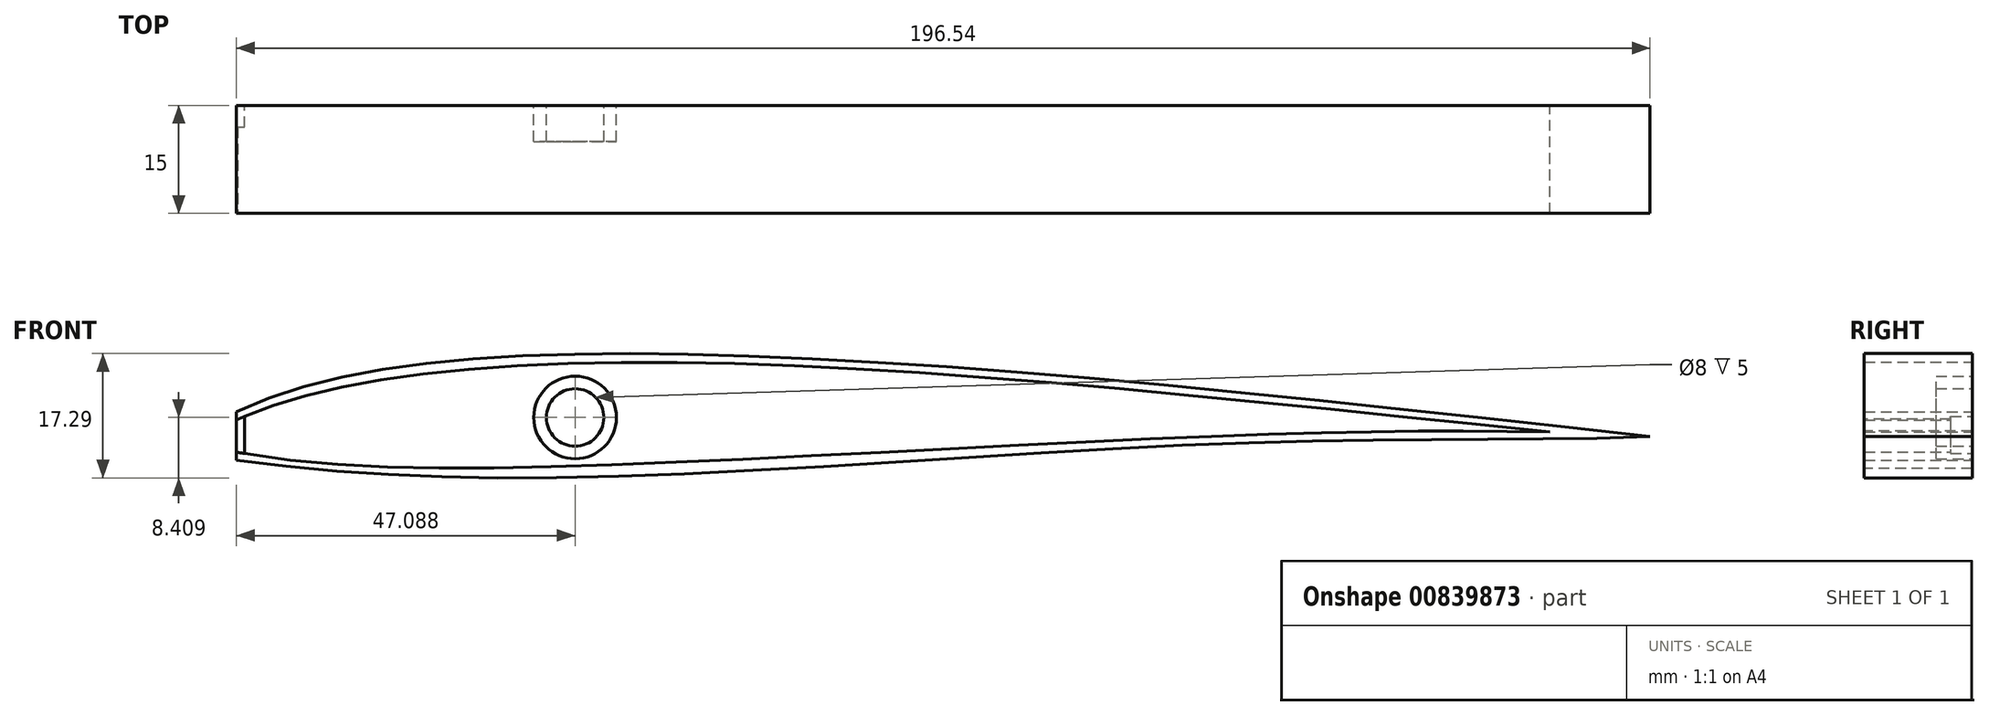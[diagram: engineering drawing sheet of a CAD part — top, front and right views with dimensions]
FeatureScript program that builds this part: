
annotation { "Feature Type Name" : "Feature", "Feature Type Description" : "" }
export const myFeature = defineFeature(function(context is Context, id is Id, definition is map)
    precondition{}
    {
        {
            var Q0;
            Q0=qCreatedBy(makeId("Front.planeOp"),FACE);
            var sketch = newSketch(context, id + "F0", { "sketchPlane" : qUnion([Q0])});
            skPoint(sketch, "E0.middle", {"position": v(0, 0) * mm});
            skFitSpline(sketch, "E1", {"points": [v(-96.98, -0.81) * mm, v(-45.24, 7.5) * mm, v(100, -4.05) * mm], "startDerivative": vector(97.58, 47.67) * mm, "endDerivative": vector(275.05, -31.29) * mm});
            skFitSpline(sketch, "E2", {"points": [v(-96.54, -7.34) * mm, v(-44.56, -9.6) * mm, v(41.7, -4.97) * mm, v(100, -4.05) * mm], "startDerivative": vector(159.07, -20.98) * mm, "endDerivative": vector(169.88, 6) * mm});
            skFitSpline(sketch, "E3", {"points": [v(-96.34, -1.64) * mm, v(-45.34, 6.27) * mm, v(86.1, -3.38) * mm], "startDerivative": vector(82.57, 38.4) * mm, "endDerivative": vector(239.73, -24.74) * mm});
            skFitSpline(sketch, "E4", {"points": [v(-97.38, -6.05) * mm, v(-44.49, -7.96) * mm, v(41.39, -3.9) * mm, v(86.1, -3.38) * mm], "startDerivative": vector(144.05, -26.77) * mm, "endDerivative": vector(139.27, -2.3) * mm});
            skLineSegment(sketch, "E5", {"start": v(-95.4, -1.21) * mm, "end": v(-95.4, -6.4) * mm});
            skLineSegment(sketch, "E6", {"start": v(-96.54, -0.6) * mm, "end": v(-96.54, -7.34) * mm});
            skFitSpline(sketch, "E7.trimOffspring", {"points": [v(-97.38, -6.05) * mm, v(-99.95, -4.56) * mm, v(-96.34, -1.64) * mm], "startDerivative": vector(-8.62, 1.03) * mm, "endDerivative": vector(10.24, 4.38) * mm});
            skPoint(sketch, "E8.trimOffspring.center.orphan", {"position": v(-96.34, -4.05) * mm});
            skPoint(sketch, "E9.1.internal.orphan", {"position": v(-101.41, -5) * mm});
            skPoint(sketch, "E10.start.orphan", {"position": v(-99.95, -4.05) * mm});
            skCircle(sketch, "E11", {"center": v(-49.45, -1.37) * mm, "radius": 4 * mm});
            skCircle(sketch, "E12", {"center": v(33.78, -1.03) * mm, "radius": 2.5 * mm});
            skLineSegment(sketch, "E13", {"start": v(-56.42, 4.45) * mm, "end": v(-56.42, -7.2) * mm});
            skLineSegment(sketch, "E14", {"start": v(-94.27, -1.68) * mm, "end": v(-94.27, -5.45) * mm});
            skFitSpline(sketch, "E15", {"points": [v(-94.27, -1.68) * mm, v(-75.44, 3) * mm, v(-56.42, 4.45) * mm], "startDerivative": vector(37.23, 13.11) * mm, "endDerivative": vector(37.06, -0.15) * mm});
            skFitSpline(sketch, "E16", {"points": [v(-56.42, -7.2) * mm, v(-75.86, -7.2) * mm, v(-94.27, -5.45) * mm], "startDerivative": vector(-38.67, -0.9) * mm, "endDerivative": vector(-37.01, 4.45) * mm});
            skLineSegment(sketch, "E17", {"start": v(-90.05, -0.3) * mm, "end": v(-86.02, -6.4) * mm});
            skLineSegment(sketch, "E18", {"start": v(-83.6, -6.64) * mm, "end": v(-75.44, 3) * mm});
            skLineSegment(sketch, "E19", {"start": v(-73.9, 3.22) * mm, "end": v(-66.47, -7.38) * mm});
            skLineSegment(sketch, "E20", {"start": v(-62.95, -7.36) * mm, "end": v(-56.42, 4.45) * mm});
            skLineSegment(sketch, "E21", {"start": v(-72.03, 3.47) * mm, "end": v(-64.9, -6.69) * mm});
            skLineSegment(sketch, "E22", {"start": v(-64.9, -6.69) * mm, "end": v(-58.76, 4.43) * mm});
            skLineSegment(sketch, "E23", {"start": v(-88.04, 0.29) * mm, "end": v(-84.32, -5.34) * mm});
            skLineSegment(sketch, "E24", {"start": v(-84.32, -5.34) * mm, "end": v(-77.56, 2.64) * mm});
            skFitSpline(sketch, "E25.trimOffspring", {"points": [v(-94.27, -1.68) * mm, v(-75.44, 3) * mm, v(-56.42, 4.45) * mm], "startDerivative": vector(37.23, 13.11) * mm, "endDerivative": vector(37.06, -0.15) * mm});
            skLineSegment(sketch, "E26", {"start": v(-39.23, 5.3) * mm, "end": v(-39.23, -6.51) * mm});
            skLineSegment(sketch, "E27", {"start": v(28.07, 1.28) * mm, "end": v(28.07, -3.67) * mm});
            skFitSpline(sketch, "E28", {"points": [v(-39.23, 5.3) * mm, v(-6.24, 3.91) * mm, v(28.07, 1.28) * mm], "startDerivative": vector(66.36, -2.2) * mm, "endDerivative": vector(68.23, -5.84) * mm});
            skFitSpline(sketch, "E29", {"points": [v(28.07, -3.67) * mm, v(-6.7, -5.32) * mm, v(-39.23, -6.51) * mm], "startDerivative": vector(-68.96, -3.46) * mm, "endDerivative": vector(-65.62, -2.21) * mm});
            skLineSegment(sketch, "E30", {"start": v(-39.23, -6.51) * mm, "end": v(-29.4, 4.97) * mm});
            skLineSegment(sketch, "E31", {"start": v(-27.29, 4.89) * mm, "end": v(-21.61, -5.9) * mm});
            skLineSegment(sketch, "E32", {"start": v(-21.48, -5.9) * mm, "end": v(-15.64, 4.4) * mm});
            skLineSegment(sketch, "E33", {"start": v(-36.65, -6.42) * mm, "end": v(-28.28, 3.34) * mm});
            skLineSegment(sketch, "E34", {"start": v(-28.28, 3.34) * mm, "end": v(-23.39, -5.97) * mm});
            skLineSegment(sketch, "E35", {"start": v(-19.55, -5.83) * mm, "end": v(-14.5, 3.08) * mm});
            skLineSegment(sketch, "E36", {"start": v(-14.5, 3.08) * mm, "end": v(-10, -5.46) * mm});
            skLineSegment(sketch, "E37", {"start": v(-8.67, -5.4) * mm, "end": v(-13.79, 4.32) * mm});
            skLineSegment(sketch, "E38", {"start": v(-8.67, -5.4) * mm, "end": v(-1.68, 3.63) * mm});
            skLineSegment(sketch, "E39", {"start": v(0, 3.51) * mm, "end": v(6.1, -4.75) * mm});
            skLineSegment(sketch, "E40", {"start": v(-6.6, -5.32) * mm, "end": v(-0.65, 2.36) * mm});
            skLineSegment(sketch, "E41", {"start": v(-0.65, 2.36) * mm, "end": v(4.65, -4.82) * mm});
            skLineSegment(sketch, "E42", {"start": v(6.1, -4.75) * mm, "end": v(10.79, 2.72) * mm});
            skLineSegment(sketch, "E43", {"start": v(13.16, 2.53) * mm, "end": v(16.11, -4.27) * mm});
            skLineSegment(sketch, "E44", {"start": v(16.11, -4.27) * mm, "end": v(20.3, 1.94) * mm});
            skLineSegment(sketch, "E45", {"start": v(23.71, 1.65) * mm, "end": v(28.07, -3.67) * mm});
            skLineSegment(sketch, "E46", {"start": v(8, -4.66) * mm, "end": v(11.98, 1.67) * mm});
            skLineSegment(sketch, "E47", {"start": v(11.98, 1.67) * mm, "end": v(14.6, -4.34) * mm});
            skLineSegment(sketch, "E48", {"start": v(18.33, -4.16) * mm, "end": v(22.07, 1.37) * mm});
            skLineSegment(sketch, "E49", {"start": v(22.07, 1.37) * mm, "end": v(26.27, -3.76) * mm});
            skCircle(sketch, "E50", {"center": v(-49.45, -1.37) * mm, "radius": 5.75 * mm});
            skSolve(sketch);
        }
        {
            var Q0;
            Q0=makeQuery(id+"F0.imprint","IMPRINT",FACE,{"disambiguationData":[TD([[makeQuery(id+"F0.imprint","IMPRINT",EDGE,{"derivedFrom":sQuery(id+"F0.wireOp",EDGE,"E3")}),-1.0]])]});
            extrude(context, id + "F1", {"entities" : qUnion([Q0]), "depth" : 3 * mm, "offsetDistance" : 25 * mm});
        }
        {
            var Q0;
            {var subQ1=sQuery(id+"F0.wireOp",EDGE,"E1");Q0=makeQuery(id+"F0.imprint","IMPRINT",FACE,{"disambiguationData":[TD([[makeQuery(id+"F0.imprint","IMPRINT",EDGE,{"derivedFrom":subQ1}),-1.0]])]});}
            extrude(context, id + "F2", {"entities" : qUnion([Q0]), "operationType" : NewBodyOperationType.ADD, "depth" : 15 * mm, "offsetDistance" : 25 * mm});
        }
        {
            var Q0;
            Q0=makeQuery(id+"F0.imprint","IMPRINT",FACE,{"disambiguationData":[TD([[makeQuery(id+"F0.imprint","IMPRINT",EDGE,{"derivedFrom":sQuery(id+"F0.wireOp",EDGE,"E11")}),-1.0]])]});
            extrude(context, id + "F3", {"entities" : qUnion([Q0]), "operationType" : NewBodyOperationType.ADD, "depth" : 5 * mm, "offsetDistance" : 25 * mm});
        }
    });
